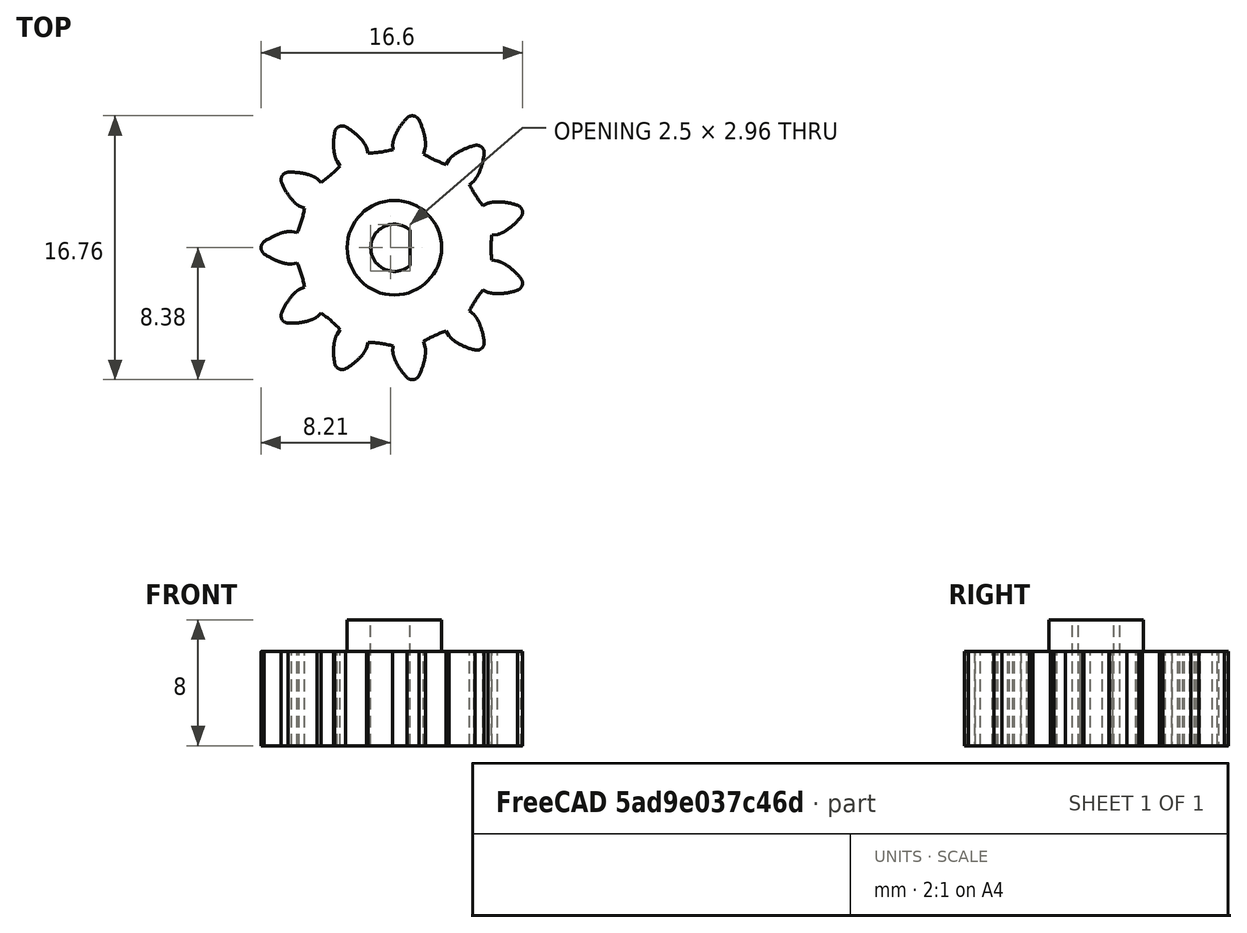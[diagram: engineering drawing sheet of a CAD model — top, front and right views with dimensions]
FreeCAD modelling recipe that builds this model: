
FCSTD DOCUMENT
Label: small_gear
License: CC-BY 3.0
LicenseURL: http://creativecommons.org/licenses/by/3.0/
objects: Part::Cylinder×2, Part::Cut×2, Part::Part2DObjectPython×1, Part::Box×1, PartDesign::Pad×1, Part::MultiFuse×1
note: 9 computed .brp shape members not serialized (recipe doc carries the construction recipe); baked Part::Feature solids carry a one-line shape summary decoded from their .brp

FEATURE [Part::Part2DObjectPython] MainGear  # Draft 2D object (typed FeaturePython)
  ExternalGear = false
  HighPrecision = true
  Modules = 1.27324
  NumberOfTeeth = 11
  PressureAngle = 20
FEATURE [Part::Cylinder] Cylinder
  Angle = 360
  Height = 11
  Placement = pos=(0,0,-2) rot=(0,0,1;0rad)
  Radius = 1.5
FEATURE [Part::Box] Box
  Height = 15
  Length = 10
  Placement = pos=(1,-5,-4) rot=(0,0,1;0rad)
  Width = 10
FEATURE [Part::Cut] Cut
  Base = -> Cylinder
  Tool = -> Box
FEATURE [PartDesign::Pad] Pad
  Length = 6
  Length2 = 100
  Sketch = -> MainGear
  Type = 0
FEATURE [Part::Cylinder] Cylinder001
  Angle = 360
  Height = 7
  Placement = pos=(0,0,1) rot=(0,0,1;0rad)
  Radius = 3
FEATURE [Part::MultiFuse] Fusion
  Shapes = -> [Pad,Cylinder001]
FEATURE [Part::Cut] Cut001
  Base = -> Fusion
  Tool = -> Cut
